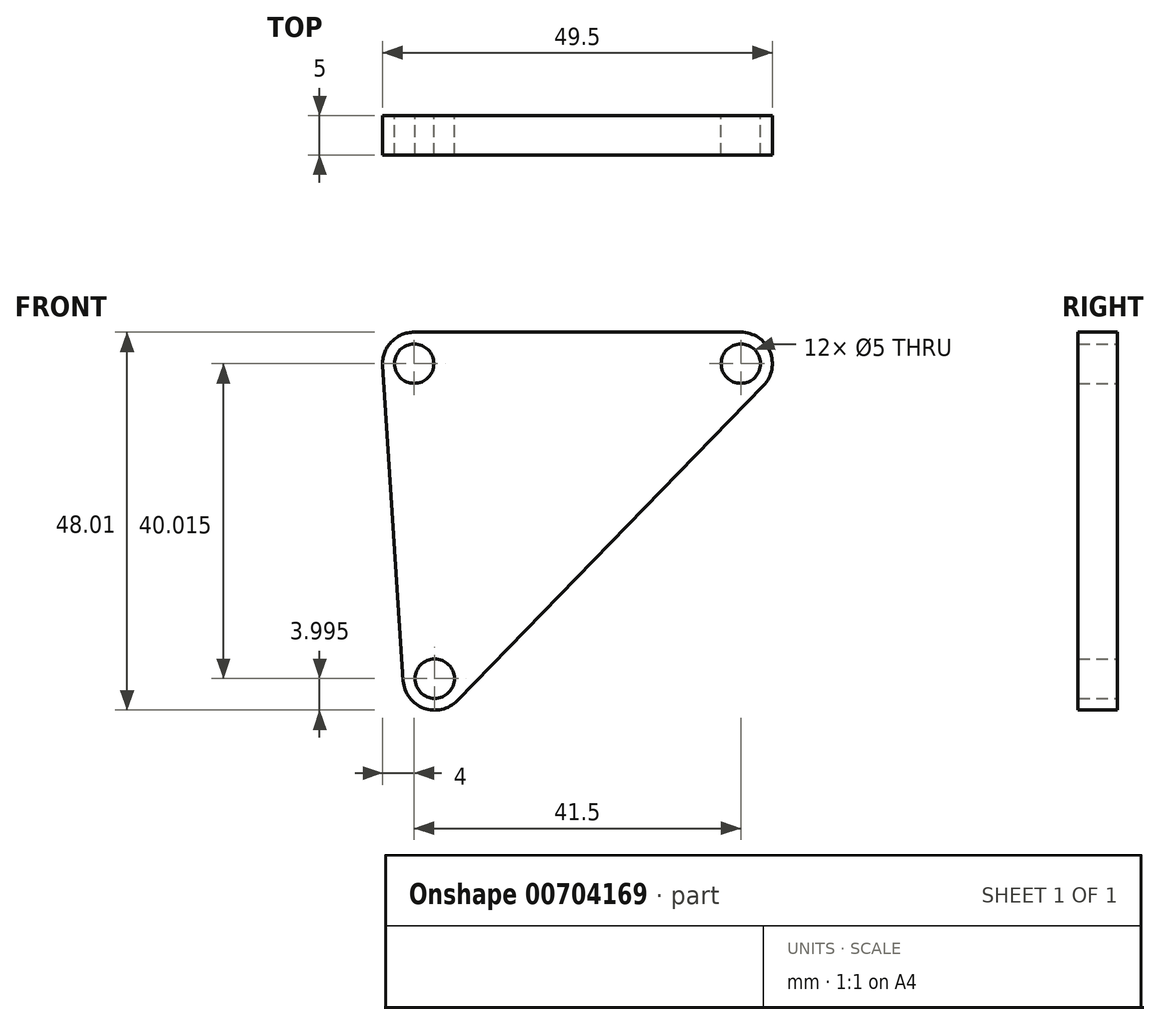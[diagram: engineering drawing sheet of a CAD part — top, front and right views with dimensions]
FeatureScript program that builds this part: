
annotation { "Feature Type Name" : "Feature", "Feature Type Description" : "" }
export const myFeature = defineFeature(function(context is Context, id is Id, definition is map)
    precondition{}
    {
        {
            var Q0;
            Q0=qCreatedBy(makeId("Front.planeOp"),FACE);
            var sketch = newSketch(context, id + "F0", { "sketchPlane" : qUnion([Q0])});
            skLineSegment(sketch, "E0", {"start": v(0, 0) * mm, "end": v(-41.5, 0) * mm, "construction": true});
            skLineSegment(sketch, "E1", {"start": v(-41.5, 0) * mm, "end": v(-38.9, -40.01) * mm, "construction": true});
            skLineSegment(sketch, "E2", {"start": v(-38.9, -40.01) * mm, "end": v(0, 0) * mm, "construction": true});
            skArc(sketch, "E3", {"start": v(-41.5, 4) * mm, "mid": v(-44.42, 2.73) * mm, "end": v(-45.5, -0.26) * mm});
            skArc(sketch, "E4", {"start": v(2.87, -2.79) * mm, "mid": v(3.68, 1.56) * mm, "end": v(0, 4) * mm});
            skArc(sketch, "E5", {"start": v(-42.88, -40.28) * mm, "mid": v(-40.27, -43.77) * mm, "end": v(-36.02, -42.8) * mm});
            skLineSegment(sketch, "E6.0", {"start": v(0, 4) * mm, "end": v(-41.5, 4) * mm});
            skLineSegment(sketch, "E6.1", {"start": v(-36.02, -42.8) * mm, "end": v(2.87, -2.79) * mm});
            skLineSegment(sketch, "E6.2", {"start": v(-45.5, -0.26) * mm, "end": v(-42.88, -40.28) * mm});
            skCircle(sketch, "E7", {"center": v(-41.5, 0) * mm, "radius": 2.5 * mm});
            skCircle(sketch, "E8", {"center": v(0, 0) * mm, "radius": 2.5 * mm});
            skCircle(sketch, "E9", {"center": v(-38.9, -40.01) * mm, "radius": 2.5 * mm});
            skSolve(sketch);
        }
        {
            var Q0;
            Q0=makeQuery(id+"F0.imprint","IMPRINT",FACE,{"disambiguationData":[TD([[makeQuery(id+"F0.imprint","IMPRINT",EDGE,{"derivedFrom":sQuery(id+"F0.wireOp",EDGE,"E3")}),1.0]])]});
            extrude(context, id + "F1", {"entities" : qUnion([Q0]), "depth" : 5 * mm, "offsetDistance" : 25 * mm});
        }
    });
